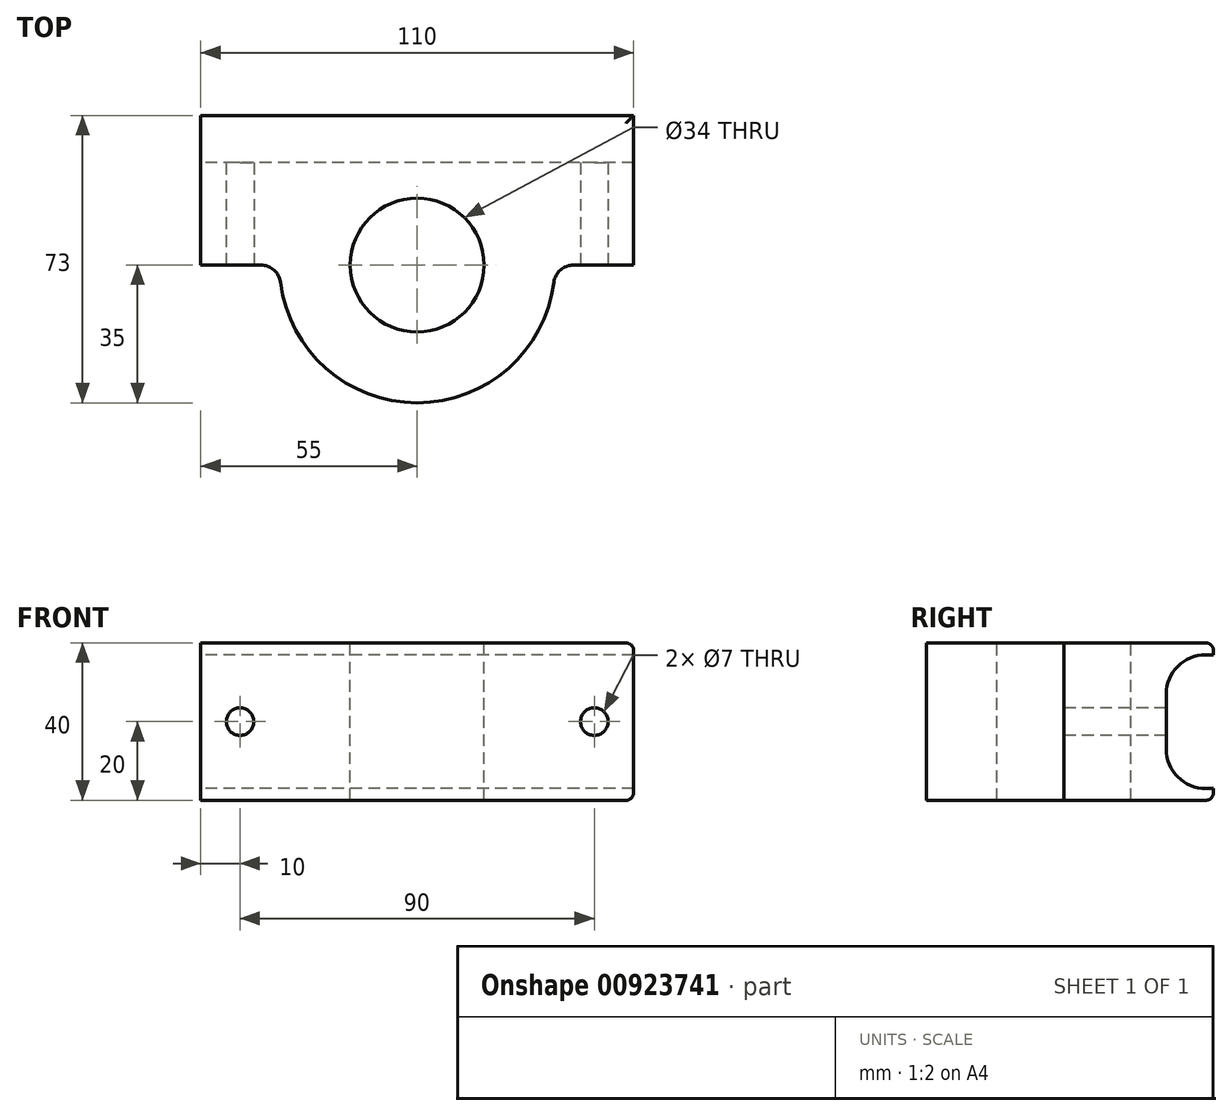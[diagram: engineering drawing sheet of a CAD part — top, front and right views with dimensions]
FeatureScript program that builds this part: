
annotation { "Feature Type Name" : "Feature", "Feature Type Description" : "" }
export const myFeature = defineFeature(function(context is Context, id is Id, definition is map)
    precondition{}
    {
        {
            var Q0;
            Q0=qCreatedBy(makeId("Right.planeOp"),FACE);
            var sketch = newSketch(context, id + "F0", { "sketchPlane" : qUnion([Q0]), "disableImprinting" : false});
            skLineSegment(sketch, "E0", {"start": v(0, 17) * mm, "end": v(0, 20) * mm});
            skLineSegment(sketch, "E1", {"start": v(0, 20) * mm, "end": v(-73, 20) * mm});
            skLineSegment(sketch, "E2", {"start": v(-73, 20) * mm, "end": v(-73, -20) * mm});
            skLineSegment(sketch, "E3", {"start": v(-73, -20) * mm, "end": v(0, -20) * mm});
            skLineSegment(sketch, "E4", {"start": v(0, 17) * mm, "end": v(-2, 17) * mm});
            skLineSegment(sketch, "E5", {"start": v(-12, 7) * mm, "end": v(-12, -7) * mm});
            skLineSegment(sketch, "E6", {"start": v(-2, -17) * mm, "end": v(0, -17) * mm});
            skPoint(sketch, "E7.0.visualSharp", {"position": v(-12, 17) * mm});
            skArc(sketch, "E7.0.filletArc", {"start": v(-2, 17) * mm, "mid": v(-9.07, 14.07) * mm, "end": v(-12, 7) * mm});
            skPoint(sketch, "E8.0.visualSharp", {"position": v(-12, -17) * mm});
            skArc(sketch, "E8.0.filletArc", {"start": v(-12, -7) * mm, "mid": v(-9.07, -14.07) * mm, "end": v(-2, -17) * mm});
            skLineSegment(sketch, "E9", {"start": v(0, -20) * mm, "end": v(0, -17) * mm});
            skSolve(sketch);
        }
        {
            var Q0;
            Q0=qSketchRegion(id+"F0",true);
            extrude(context, id + "F1", {"entities" : qUnion([Q0]), "flatOperationType" : FlatOperationType.REMOVE, "depth" : 110 * mm, "offsetDistance" : 25 * mm, "symmetric" : true, "domain" : OperationDomain.MODEL});
        }
        {
            var Q0;
            Q0=makeQuery(id+"F1.opExtrude","SWEPT_FACE",FACE,{"disambiguationData":[OSD([sQuery(id+"F0.wireOp",EDGE,"E1")])]});
            var sketch = newSketch(context, id + "F2", { "sketchPlane" : qUnion([Q0])});
            skLineSegment(sketch, "E10.0", {"start": v(-55, -38) * mm, "end": v(-55, -73) * mm});
            skLineSegment(sketch, "E11.0", {"start": v(55, -38) * mm, "end": v(55, -73) * mm});
            skLineSegment(sketch, "E12", {"start": v(-55, -38) * mm, "end": v(-35, -38) * mm});
            skArc(sketch, "E13", {"start": v(-35, -38) * mm, "mid": v(0, -73) * mm, "end": v(35, -38) * mm});
            skLineSegment(sketch, "E14", {"start": v(35, -38) * mm, "end": v(55, -38) * mm});
            skPoint(sketch, "E15.orphan", {"position": v(-55, 0) * mm});
            skPoint(sketch, "E16.orphan", {"position": v(55, 0) * mm});
            skCircle(sketch, "E17", {"center": v(0, -38) * mm, "radius": 17 * mm});
            skSolve(sketch);
        }
        {
            var Q0;
            Q0=qSketchRegion(id+"F2",true);
            var Q1;
            {var subQ0=sQuery(id+"F2.wireOp",EDGE,"E11.0");Q1=makeQuery(id+"F2.imprint","IMPRINT",FACE,{"disambiguationData":[TD([[makeQuery(id+"F2.imprint","IMPRINT",EDGE,{"derivedFrom":subQ0}),-1.0]])]});}
            var Q2;
            {var subQ0=sQuery(id+"F2.wireOp",EDGE,"E10.0");Q2=makeQuery(id+"F2.imprint","IMPRINT",FACE,{"disambiguationData":[TD([[makeQuery(id+"F2.imprint","IMPRINT",EDGE,{"derivedFrom":subQ0}),1.0]])]});}
            extrude(context, id + "F3", {"entities" : qUnion([Q0, Q1, Q2]), "operationType" : NewBodyOperationType.REMOVE, "endBound" : BoundingType.THROUGH_ALL, "oppositeDirection" : true, "depth" : 25 * mm, "offsetDistance" : 25 * mm});
        }
        {
            var Q0;
            Q0=makeQuery(id+"F3.boolean.opBoolean","COPY",EDGE,{"derivedFrom":makeQuery(id+"F3.opExtrude","SWEPT_EDGE",EDGE,{"disambiguationData":[OSD([sQuery(id+"F2.wireOp",EDGE,"E13"),sQuery(id+"F2.wireOp",EDGE,"E14")])]})});
            var Q1;
            Q1=makeQuery(id+"F3.boolean.opBoolean","COPY",EDGE,{"derivedFrom":makeQuery(id+"F3.opExtrude","SWEPT_EDGE",EDGE,{"disambiguationData":[OSD([sQuery(id+"F0.wireOp",EDGE,"E1"),sQuery(id+"F2.wireOp",EDGE,"E11.0"),sQuery(id+"F2.wireOp",EDGE,"E14")])]})});
            var Q2;
            Q2=makeQuery(id+"F3.boolean.opBoolean","COPY",EDGE,{"derivedFrom":makeQuery(id+"F3.opExtrude","SWEPT_EDGE",EDGE,{"disambiguationData":[OSD([sQuery(id+"F0.wireOp",EDGE,"E1"),sQuery(id+"F2.wireOp",EDGE,"E10.0"),sQuery(id+"F2.wireOp",EDGE,"E12")])]})});
            var Q3;
            Q3=makeQuery(id+"F3.boolean.opBoolean","COPY",EDGE,{"derivedFrom":makeQuery(id+"F3.opExtrude","SWEPT_EDGE",EDGE,{"disambiguationData":[OSD([sQuery(id+"F2.wireOp",EDGE,"E12"),sQuery(id+"F2.wireOp",EDGE,"E13")])]})});
            fillet(context, id + "F4", {"entities" : qUnion([Q0, Q1, Q2, Q3]), "tangentPropagation" : true, "radius" : 5 * mm, "defaultsChanged" : false, "vertexSettings" : [], "allowEdgeOverflow" : false});
        }
        {
            var Q0;
            Q0=makeQuery(id+"F3.boolean.opBoolean","COPY",FACE,{"derivedFrom":makeQuery(id+"F3.opExtrude","SWEPT_FACE",FACE,{"disambiguationData":[OSD([sQuery(id+"F2.wireOp",EDGE,"E12")])]})});
            var sketch = newSketch(context, id + "F5", { "sketchPlane" : qUnion([Q0]), "disableImprinting" : false});
            skCircle(sketch, "E18", {"center": v(-45, 0) * mm, "radius": 3.5 * mm});
            skCircle(sketch, "E19.1.0.0", {"center": v(45, 0) * mm, "radius": 3.5 * mm});
            skLineSegment(sketch, "E19.direction1", {"start": v(-45, 0) * mm, "end": v(45, 0) * mm, "construction": true});
            skSolve(sketch);
        }
        {
            var Q0;
            Q0=qSketchRegion(id+"F5",true);
            extrude(context, id + "F6", {"entities" : qUnion([Q0]), "operationType" : NewBodyOperationType.REMOVE, "endBound" : BoundingType.UP_TO_NEXT, "oppositeDirection" : true, "depth" : 25 * mm, "offsetDistance" : 25 * mm});
        }
        {
            var Q0;
            Q0=makeQuery(id+"F1.opExtrude","SWEPT_EDGE",EDGE,{"disambiguationData":[OSD([sQuery(id+"F0.wireOp",EDGE,"E0"),sQuery(id+"F0.wireOp",EDGE,"E1")])]});
            var Q1;
            Q1=makeQuery(id+"F1.opExtrude","SWEPT_EDGE",EDGE,{"disambiguationData":[OSD([sQuery(id+"F0.wireOp",EDGE,"E3"),sQuery(id+"F0.wireOp",EDGE,"FGgDNANv-2lG2-2nwa-Lqix-LXMTOSNKBAt1")])]});
            var Q2;
            Q2=makeQuery(id+"F1.opExtrude","CAP_EDGE",EDGE,{"disambiguationData":[OSD([sQuery(id+"F0.wireOp",EDGE,"E1")])],"isStart":false});
            var Q3;
            Q3=makeQuery(id+"F1.opExtrude","CAP_EDGE",EDGE,{"disambiguationData":[OSD([sQuery(id+"F0.wireOp",EDGE,"E3")])],"isStart":false});
            fillet(context, id + "F7", {"entities" : qUnion([Q0, Q1, Q2, Q3]), "tangentPropagation" : true, "radius" : 2 * mm, "defaultsChanged" : false, "vertexSettings" : [], "allowEdgeOverflow" : false});
        }
    });
